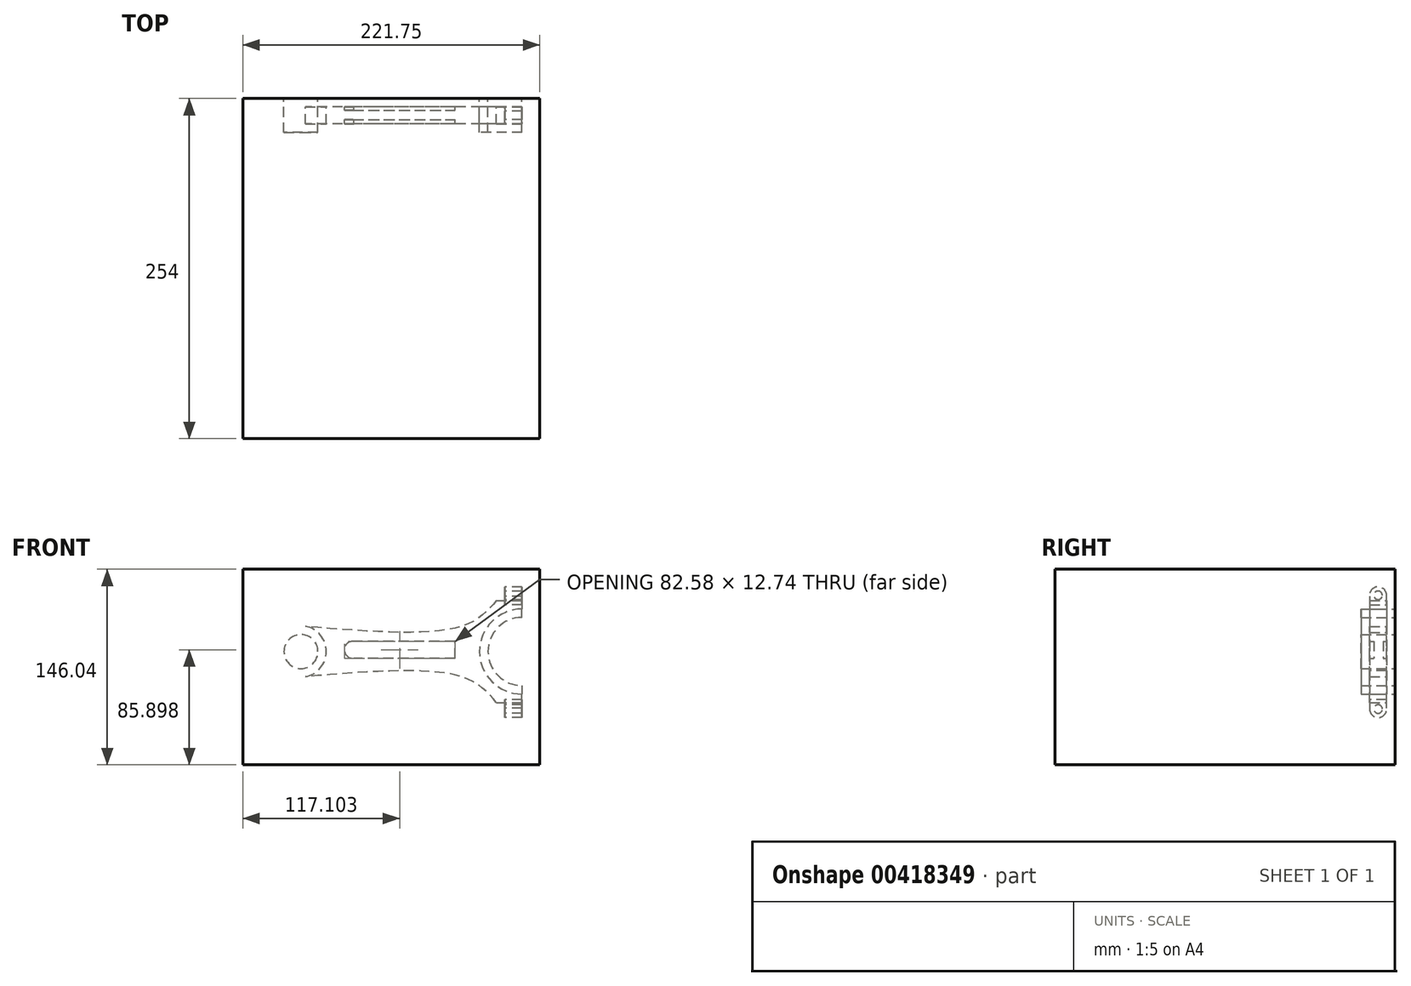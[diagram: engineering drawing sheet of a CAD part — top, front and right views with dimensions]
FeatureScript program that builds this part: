
annotation { "Feature Type Name" : "Feature", "Feature Type Description" : "" }
export const myFeature = defineFeature(function(context is Context, id is Id, definition is map)
    precondition{}
    {
        {
            var Q0;
            Q0=qCreatedBy(makeId("Front.planeOp"),FACE);
            var sketch = newSketch(context, id + "F0", { "sketchPlane" : qUnion([Q0])});
            skLineSegment(sketch, "E0", {"start": v(0, 6.39) * mm, "end": v(76.2, 6.36) * mm});
            skPoint(sketch, "E1", {"position": v(127, 0) * mm});
            skArc(sketch, "E2", {"start": v(127, 25.4) * mm, "mid": v(109.04, 17.96) * mm, "end": v(101.6, 0) * mm});
            skArc(sketch, "E3", {"start": v(127, 31.75) * mm, "mid": v(104.55, 22.45) * mm, "end": v(95.25, 0) * mm});
            skLineSegment(sketch, "E4", {"start": v(127, 25.4) * mm, "end": v(127, 31.75) * mm});
            skPoint(sketch, "E5", {"position": v(127, 38.1) * mm});
            skPoint(sketch, "E6", {"position": v(114.3, 38.1) * mm});
            skArc(sketch, "E7", {"start": v(0, 6.39) * mm, "mid": v(-4.52, 4.52) * mm, "end": v(-6.39, 0) * mm});
            skArc(sketch, "E8", {"start": v(-57.15, 0) * mm, "mid": v(-38.1, 19.05) * mm, "end": v(-19.05, 0) * mm});
            skArc(sketch, "E9", {"start": v(-50.8, 0) * mm, "mid": v(-38.1, 12.7) * mm, "end": v(-25.4, 0) * mm});
            skArc(sketch, "E10", {"start": v(82.55, 0) * mm, "mid": v(80.7, 4.5) * mm, "end": v(76.2, 6.35) * mm});
            skPoint(sketch, "E11", {"position": v(127, 31.75) * mm});
            skPoint(sketch, "E12", {"position": v(107.95, 38.1) * mm});
            skPoint(sketch, "E13", {"position": v(82.55, 6.36) * mm});
            skPoint(sketch, "E14", {"position": v(82.55, 19.05) * mm});
            skFitSpline(sketch, "E15", {"points": [v(107.95, 38.1) * mm, v(82.55, 19.05) * mm, v(-38.1, 19.05) * mm], "startDerivative": vector(-56.67, -65.71) * mm, "endDerivative": vector(-218.11, 18.57) * mm});
            skLineSegment(sketch, "E16", {"start": v(107.95, 38.1) * mm, "end": v(114.3, 38.1) * mm});
            skLineSegment(sketch, "E17.bottom", {"start": v(114.3, 38.1) * mm, "end": v(127, 38.1) * mm});
            skLineSegment(sketch, "E17.top", {"start": v(114.3, 50.74) * mm, "end": v(127, 50.74) * mm});
            skLineSegment(sketch, "E17.left", {"start": v(114.3, 38.1) * mm, "end": v(114.3, 50.74) * mm});
            skLineSegment(sketch, "E17.right", {"start": v(127, 38.1) * mm, "end": v(127, 50.74) * mm});
            skLineSegment(sketch, "E18", {"start": v(127, 38.1) * mm, "end": v(127, 31.75) * mm});
            skLineSegment(sketch, "E19.MirrorCS", {"start": v(127, -38.1) * mm, "end": v(127, -31.75) * mm});
            skLineSegment(sketch, "E20.MirrorCS", {"start": v(107.95, -38.1) * mm, "end": v(114.3, -38.1) * mm});
            skLineSegment(sketch, "E21.MirrorCS", {"start": v(127, -25.4) * mm, "end": v(127, -31.75) * mm});
            skArc(sketch, "E22.MirrorCS", {"start": v(0, -6.39) * mm, "mid": v(-4.52, -4.52) * mm, "end": v(-6.39, 0) * mm});
            skLineSegment(sketch, "E23.MirrorCS", {"start": v(114.3, -50.74) * mm, "end": v(127, -50.74) * mm});
            skArc(sketch, "E24.MirrorCS", {"start": v(82.55, 0) * mm, "mid": v(80.7, -4.5) * mm, "end": v(76.2, -6.35) * mm});
            skLineSegment(sketch, "E25.MirrorCS", {"start": v(114.3, -38.1) * mm, "end": v(127, -38.1) * mm});
            skLineSegment(sketch, "E26.MirrorCS", {"start": v(127, -38.1) * mm, "end": v(127, -50.74) * mm});
            skPoint(sketch, "E27.MirrorP", {"position": v(107.95, -38.1) * mm});
            skFitSpline(sketch, "E28.MirrorCS", {"points": [v(107.95, -38.1) * mm, v(82.55, -19.05) * mm, v(-38.1, -19.05) * mm], "startDerivative": vector(-56.67, 65.71) * mm, "endDerivative": vector(-218.11, -18.57) * mm});
            skLineSegment(sketch, "E29.MirrorCS", {"start": v(0, -6.39) * mm, "end": v(76.2, -6.36) * mm});
            skLineSegment(sketch, "E30.MirrorCS", {"start": v(114.3, -38.1) * mm, "end": v(114.3, -50.74) * mm});
            skArc(sketch, "E31.MirrorCS", {"start": v(127, -25.4) * mm, "mid": v(109.04, -17.96) * mm, "end": v(101.6, 0) * mm});
            skPoint(sketch, "E32.MirrorP", {"position": v(127, -38.1) * mm});
            skPoint(sketch, "E33.MirrorP", {"position": v(127, -31.75) * mm});
            skPoint(sketch, "E34.MirrorP", {"position": v(82.55, -6.36) * mm});
            skPoint(sketch, "E35.MirrorP", {"position": v(114.3, -38.1) * mm});
            skArc(sketch, "E36.MirrorCS", {"start": v(-50.8, 0) * mm, "mid": v(-38.1, -12.7) * mm, "end": v(-25.4, 0) * mm});
            skArc(sketch, "E37.MirrorCS", {"start": v(127, -31.75) * mm, "mid": v(104.55, -22.45) * mm, "end": v(95.25, 0) * mm});
            skArc(sketch, "E38.MirrorCS", {"start": v(-57.15, 0) * mm, "mid": v(-38.1, -19.05) * mm, "end": v(-19.05, 0) * mm});
            skSolve(sketch);
        }
        {
            var Q0;
            Q0=makeQuery(id+"F0.imprint","IMPRINT",FACE,{"disambiguationData":[TD([[makeQuery(id+"F0.imprint","IMPRINT",EDGE,{"derivedFrom":sQuery(id+"F0.wireOp",EDGE,"E9")}),1.0]])]});
            var Q1;
            Q1=makeQuery(id+"F0.imprint","IMPRINT",FACE,{"disambiguationData":[TD([[makeQuery(id+"F0.imprint","IMPRINT",EDGE,{"derivedFrom":sQuery(id+"F0.wireOp",EDGE,"E2")}),-1.0]])]});
            extrude(context, id + "F1", {"entities" : qUnion([Q0, Q1]), "depth" : 25.4 * mm});
        }
        {
            var Q0;
            Q0=makeQuery(id+"F0.imprint","IMPRINT",FACE,{"disambiguationData":[TD([[makeQuery(id+"F0.imprint","IMPRINT",EDGE,{"derivedFrom":sQuery(id+"F0.wireOp",EDGE,"E3")}),-1.0]])]});
            extrude(context, id + "F2", {"entities" : qUnion([Q0]), "depth" : 19.05 * mm, "hasSecondDirection" : true, "secondDirectionOppositeDirection" : false, "secondDirectionDepth" : 6.35 * mm});
        }
        {
            var Q0;
            Q0=sQuery(id+"F0.wireOp",EDGE,"E0");
            var Q1;
            Q1=sQuery(id+"F0.wireOp",EDGE,"E10");
            var Q2;
            Q2=sQuery(id+"F0.wireOp",EDGE,"E24.MirrorCS");
            var Q3;
            Q3=sQuery(id+"F0.wireOp",EDGE,"E29.MirrorCS");
            var Q4;
            Q4=sQuery(id+"F0.wireOp",EDGE,"E22.MirrorCS");
            var Q5;
            Q5=sQuery(id+"F0.wireOp",EDGE,"E7");
            extrude(context, id + "F3", {"bodyType" : ToolBodyType.SURFACE, "surfaceEntities" : qUnion([Q0, Q1, Q2, Q3, Q4, Q5]), "depth" : 15.88 * mm, "hasSecondDirection" : true, "secondDirectionOppositeDirection" : false, "secondDirectionDepth" : 9.52 * mm});
        }
        {
            var Q0;
            Q0=qCreatedBy(makeId("Right.planeOp"),FACE);
            var sketch = newSketch(context, id + "F4", { "sketchPlane" : qUnion([Q0])});
            skArc(sketch, "E39", {"start": v(-6.4, 38.1) * mm, "mid": v(-12.7, 45.13) * mm, "end": v(-19.02, 38.1) * mm});
            skCircle(sketch, "E40", {"center": v(-12.7, 38.78) * mm, "radius": 3.18 * mm});
            skLineSegment(sketch, "E41", {"start": v(-19.02, 38.1) * mm, "end": v(-19.02, 31.77) * mm});
            skLineSegment(sketch, "E42", {"start": v(-19.02, 31.77) * mm, "end": v(-6.32, 31.77) * mm});
            skLineSegment(sketch, "E43", {"start": v(-6.32, 31.77) * mm, "end": v(-6.4, 38.1) * mm});
            skLineSegment(sketch, "E44.MirrorCS", {"start": v(-19.02, -31.76) * mm, "end": v(-6.32, -31.76) * mm});
            skLineSegment(sketch, "E45.MirrorCS", {"start": v(-6.32, -31.76) * mm, "end": v(-6.4, -38.1) * mm});
            skLineSegment(sketch, "E46.MirrorCS", {"start": v(-19.02, -38.1) * mm, "end": v(-19.02, -31.76) * mm});
            skCircle(sketch, "E47.MirrorC", {"center": v(-12.7, -38.77) * mm, "radius": 3.18 * mm});
            skArc(sketch, "E48.MirrorCS", {"start": v(-6.4, -38.1) * mm, "mid": v(-12.7, -45.12) * mm, "end": v(-19.02, -38.1) * mm});
            skSolve(sketch);
        }
        {
            var Q0;
            Q0=makeQuery(id+"F4.imprint","IMPRINT",FACE,{"disambiguationData":[TD([[makeQuery(id+"F4.imprint","IMPRINT",EDGE,{"derivedFrom":sQuery(id+"F4.wireOp",EDGE,"E39")}),1.0]])]});
            extrude(context, id + "F5", {"entities" : qUnion([Q0]), "depth" : 12.7 * mm});
        }
        {
            var Q0;
            Q0=makeQuery(id+"F5.opExtrude","SWEPT_BODY",BODY,{"disambiguationData":[OSD([sQuery(id+"F4.wireOp",EDGE,"E39"),sQuery(id+"F4.wireOp",EDGE,"E40"),sQuery(id+"F4.wireOp",EDGE,"E41"),sQuery(id+"F4.wireOp",EDGE,"E42"),sQuery(id+"F4.wireOp",EDGE,"E43")])]});
            transform(context, id + "F6", {"entities" : qUnion([Q0]), "transformType" : TransformType.TRANSLATION_3D, "dx" : 107.95 * mm, "dy" : 0 * mm, "dz" : 3.17 * mm, "makeCopy" : false});
        }
        {
            var Q0;
            Q0=makeQuery(id+"F5.opExtrude","SWEPT_BODY",BODY,{"disambiguationData":[OSD([sQuery(id+"F4.wireOp",EDGE,"E39"),sQuery(id+"F4.wireOp",EDGE,"E40"),sQuery(id+"F4.wireOp",EDGE,"E41"),sQuery(id+"F4.wireOp",EDGE,"E42"),sQuery(id+"F4.wireOp",EDGE,"E43")])]});
            transform(context, id + "F7", {"entities" : qUnion([Q0]), "transformType" : TransformType.TRANSLATION_3D, "dx" : 0 * mm, "dy" : 0 * mm, "dz" : 0 * mm, "makeCopy" : true});
        }
        {
            var Q0;
            Q0=makeQuery(id+"F7.opPattern","COPY",BODY,{"derivedFrom":makeQuery(id+"F5.opExtrude","SWEPT_BODY",BODY,{"disambiguationData":[OSD([sQuery(id+"F4.wireOp",EDGE,"E39"),sQuery(id+"F4.wireOp",EDGE,"E40"),sQuery(id+"F4.wireOp",EDGE,"E41"),sQuery(id+"F4.wireOp",EDGE,"E42"),sQuery(id+"F4.wireOp",EDGE,"E43")])]}),"instanceName":"1"});
            transform(context, id + "F8", {"entities" : qUnion([Q0]), "transformType" : TransformType.TRANSLATION_3D, "dx" : 26.16 * mm, "dy" : 0 * mm, "dz" : -77.22 * mm, "makeCopy" : false});
        }
        {
            var Q0;
            Q0=makeQuery(id+"F7.opPattern","COPY",BODY,{"derivedFrom":makeQuery(id+"F5.opExtrude","SWEPT_BODY",BODY,{"disambiguationData":[OSD([sQuery(id+"F4.wireOp",EDGE,"E39"),sQuery(id+"F4.wireOp",EDGE,"E40"),sQuery(id+"F4.wireOp",EDGE,"E41"),sQuery(id+"F4.wireOp",EDGE,"E42"),sQuery(id+"F4.wireOp",EDGE,"E43")])]}),"instanceName":"1"});
            var Q1;
            Q1=makeQuery(id+"F7.opPattern","COPY",EDGE,{"derivedFrom":makeQuery(id+"F5.opExtrude","SWEPT_EDGE",EDGE,{"disambiguationData":[OSD([sQuery(id+"F4.wireOp",EDGE,"E39"),sQuery(id+"F4.wireOp",EDGE,"E41")])]}),"instanceName":"1"});
            transform(context, id + "F9", {"entities" : qUnion([Q0]), "transformType" : TransformType.ROTATION, "transformAxis" : qUnion([Q1]), "angle" : 180 * degree, "makeCopy" : false});
        }
        {
            var Q0;
            Q0=makeQuery(id+"F7.opPattern","COPY",BODY,{"derivedFrom":makeQuery(id+"F5.opExtrude","SWEPT_BODY",BODY,{"disambiguationData":[OSD([sQuery(id+"F4.wireOp",EDGE,"E39"),sQuery(id+"F4.wireOp",EDGE,"E40"),sQuery(id+"F4.wireOp",EDGE,"E41"),sQuery(id+"F4.wireOp",EDGE,"E42"),sQuery(id+"F4.wireOp",EDGE,"E43")])]}),"instanceName":"1"});
            transform(context, id + "F10", {"entities" : qUnion([Q0]), "transformType" : TransformType.TRANSLATION_3D, "dx" : -26.17 * mm, "dy" : 12.7 * mm, "dz" : -6.35 * mm, "makeCopy" : false});
        }
        {
            var Q0;
            Q0=qCreatedBy(makeId("Front.planeOp"),FACE);
            var sketch = newSketch(context, id + "F11", { "sketchPlane" : qUnion([Q0])});
            skArc(sketch, "E49", {"start": v(83.25, 1.25) * mm, "mid": v(81.4, 5.74) * mm, "end": v(76.9, 7.6) * mm});
            skCircle(sketch, "E50", {"center": v(76.9, 1.25) * mm, "radius": 6.35 * mm});
            skCircle(sketch, "E51", {"center": v(0.7, 1.25) * mm, "radius": 6.39 * mm});
            skLineSegment(sketch, "E52.bottom", {"start": v(0.7, 7.64) * mm, "end": v(76.9, 7.64) * mm});
            skLineSegment(sketch, "E52.top", {"start": v(0.7, -5.1) * mm, "end": v(76.9, -5.1) * mm});
            skLineSegment(sketch, "E52.left", {"start": v(0.7, 7.64) * mm, "end": v(0.7, -5.1) * mm});
            skLineSegment(sketch, "E52.right", {"start": v(76.9, 7.64) * mm, "end": v(76.9, -5.1) * mm});
            skSolve(sketch);
        }
        {
            var Q0;
            {var subQ6=sQuery(id+"F11.wireOp",EDGE,"E52.bottom");Q0=makeQuery(id+"F11.imprint","IMPRINT",FACE,{"disambiguationData":[TD([[makeQuery(id+"F11.imprint","IMPRINT",EDGE,{"derivedFrom":subQ6}),-1.0]])]});}
            var Q1;
            {var subQ0=sQuery(id+"F11.wireOp",EDGE,"E52.left");Q1=makeQuery(id+"F11.imprint","IMPRINT",FACE,{"disambiguationData":[TD([[makeQuery(id+"F11.imprint","IMPRINT",EDGE,{"derivedFrom":subQ0}),1.0]])]});}
            var Q2;
            {var subQ0=sQuery(id+"F11.wireOp",EDGE,"E52.left");Q2=makeQuery(id+"F11.imprint","IMPRINT",FACE,{"disambiguationData":[TD([[makeQuery(id+"F11.imprint","IMPRINT",EDGE,{"derivedFrom":subQ0}),-1.0]])]});}
            var Q3;
            {var subQ0=sQuery(id+"F11.wireOp",EDGE,"E52.right");var subQ1=sQuery(id+"F11.wireOp",EDGE,"E50");var subQ3=makeQuery(id+"F11.imprint","INTERSECT",VERTEX,{"derivedFrom":[subQ1,subQ0]});Q3=makeQuery(id+"F11.imprint","IMPRINT",FACE,{"disambiguationData":[TD([[makeQuery(id+"F11.imprint","IMPRINT",EDGE,{"disambiguationData":[TD([[subQ3,-1.0]])],"derivedFrom":subQ1}),1.0]])]});}
            var Q4;
            {var subQ0=sQuery(id+"F11.wireOp",EDGE,"E52.right");var subQ1=sQuery(id+"F11.wireOp",EDGE,"E50");var subQ3=makeQuery(id+"F11.imprint","INTERSECT",VERTEX,{"derivedFrom":[subQ1,subQ0]});Q4=makeQuery(id+"F11.imprint","IMPRINT",FACE,{"disambiguationData":[TD([[makeQuery(id+"F11.imprint","IMPRINT",EDGE,{"disambiguationData":[TD([[subQ3,1.0]])],"derivedFrom":subQ1}),1.0]])]});}
            extrude(context, id + "F12", {"entities" : qUnion([Q0, Q1, Q2, Q3, Q4]), "operationType" : NewBodyOperationType.REMOVE, "depth" : 22.22 * mm, "hasSecondDirection" : true, "secondDirectionOppositeDirection" : false, "secondDirectionDepth" : 15.88 * mm});
        }
        {
            var Q0;
            {var subQ6=sQuery(id+"F11.wireOp",EDGE,"E52.bottom");Q0=makeQuery(id+"F11.imprint","IMPRINT",FACE,{"disambiguationData":[TD([[makeQuery(id+"F11.imprint","IMPRINT",EDGE,{"derivedFrom":subQ6}),-1.0]])]});}
            var Q1;
            {var subQ0=sQuery(id+"F11.wireOp",EDGE,"E52.left");Q1=makeQuery(id+"F11.imprint","IMPRINT",FACE,{"disambiguationData":[TD([[makeQuery(id+"F11.imprint","IMPRINT",EDGE,{"derivedFrom":subQ0}),1.0]])]});}
            var Q2;
            {var subQ0=sQuery(id+"F11.wireOp",EDGE,"E52.left");Q2=makeQuery(id+"F11.imprint","IMPRINT",FACE,{"disambiguationData":[TD([[makeQuery(id+"F11.imprint","IMPRINT",EDGE,{"derivedFrom":subQ0}),-1.0]])]});}
            var Q3;
            {var subQ0=sQuery(id+"F11.wireOp",EDGE,"E52.right");var subQ1=sQuery(id+"F11.wireOp",EDGE,"E50");var subQ3=makeQuery(id+"F11.imprint","INTERSECT",VERTEX,{"derivedFrom":[subQ1,subQ0]});Q3=makeQuery(id+"F11.imprint","IMPRINT",FACE,{"disambiguationData":[TD([[makeQuery(id+"F11.imprint","IMPRINT",EDGE,{"disambiguationData":[TD([[subQ3,1.0]])],"derivedFrom":subQ1}),1.0]])]});}
            var Q4;
            {var subQ0=sQuery(id+"F11.wireOp",EDGE,"E52.right");var subQ1=sQuery(id+"F11.wireOp",EDGE,"E50");var subQ3=makeQuery(id+"F11.imprint","INTERSECT",VERTEX,{"derivedFrom":[subQ1,subQ0]});Q4=makeQuery(id+"F11.imprint","IMPRINT",FACE,{"disambiguationData":[TD([[makeQuery(id+"F11.imprint","IMPRINT",EDGE,{"disambiguationData":[TD([[subQ3,-1.0]])],"derivedFrom":subQ1}),1.0]])]});}
            extrude(context, id + "F13", {"entities" : qUnion([Q0, Q1, Q2, Q3, Q4]), "operationType" : NewBodyOperationType.REMOVE, "depth" : 8.9 * mm, "hasSecondDirection" : true, "secondDirectionOppositeDirection" : true, "secondDirectionDepth" : 3.17 * mm});
        }
        {
            var Q0;
            Q0=makeQuery(id+"F5.opExtrude","SWEPT_BODY",BODY,{"disambiguationData":[OSD([sQuery(id+"F4.wireOp",EDGE,"E39"),sQuery(id+"F4.wireOp",EDGE,"E40"),sQuery(id+"F4.wireOp",EDGE,"E41"),sQuery(id+"F4.wireOp",EDGE,"E42"),sQuery(id+"F4.wireOp",EDGE,"E43")])]});
            var Q1;
            Q1=makeQuery(id+"F7.opPattern","COPY",BODY,{"derivedFrom":makeQuery(id+"F5.opExtrude","SWEPT_BODY",BODY,{"disambiguationData":[OSD([sQuery(id+"F4.wireOp",EDGE,"E39"),sQuery(id+"F4.wireOp",EDGE,"E40"),sQuery(id+"F4.wireOp",EDGE,"E41"),sQuery(id+"F4.wireOp",EDGE,"E42"),sQuery(id+"F4.wireOp",EDGE,"E43")])]}),"instanceName":"1"});
            transform(context, id + "F14", {"entities" : qUnion([Q0, Q1]), "transformType" : TransformType.TRANSLATION_3D, "dx" : 6.35 * mm, "dy" : 0 * mm, "dz" : 0 * mm, "makeCopy" : false});
        }
        {
            var Q0;
            Q0=qCreatedBy(makeId("Front.planeOp"),FACE);
            var sketch = newSketch(context, id + "F15", { "sketchPlane" : qUnion([Q0])});
            skLineSegment(sketch, "E53.bottom", {"start": v(-81.5, 61.41) * mm, "end": v(140.26, 61.41) * mm});
            skLineSegment(sketch, "E53.top", {"start": v(-81.5, -84.63) * mm, "end": v(140.26, -84.63) * mm});
            skLineSegment(sketch, "E53.left", {"start": v(-81.5, 61.41) * mm, "end": v(-81.5, -84.63) * mm});
            skLineSegment(sketch, "E53.right", {"start": v(140.26, 61.41) * mm, "end": v(140.26, -84.63) * mm});
            skSolve(sketch);
        }
        {
            var Q0;
            Q0 = qSketchRegion(id + "F15", true);
            extrude(context, id + "F16", {"entities" : qUnion([Q0]), "depth" : 254 * mm});
        }
    });
